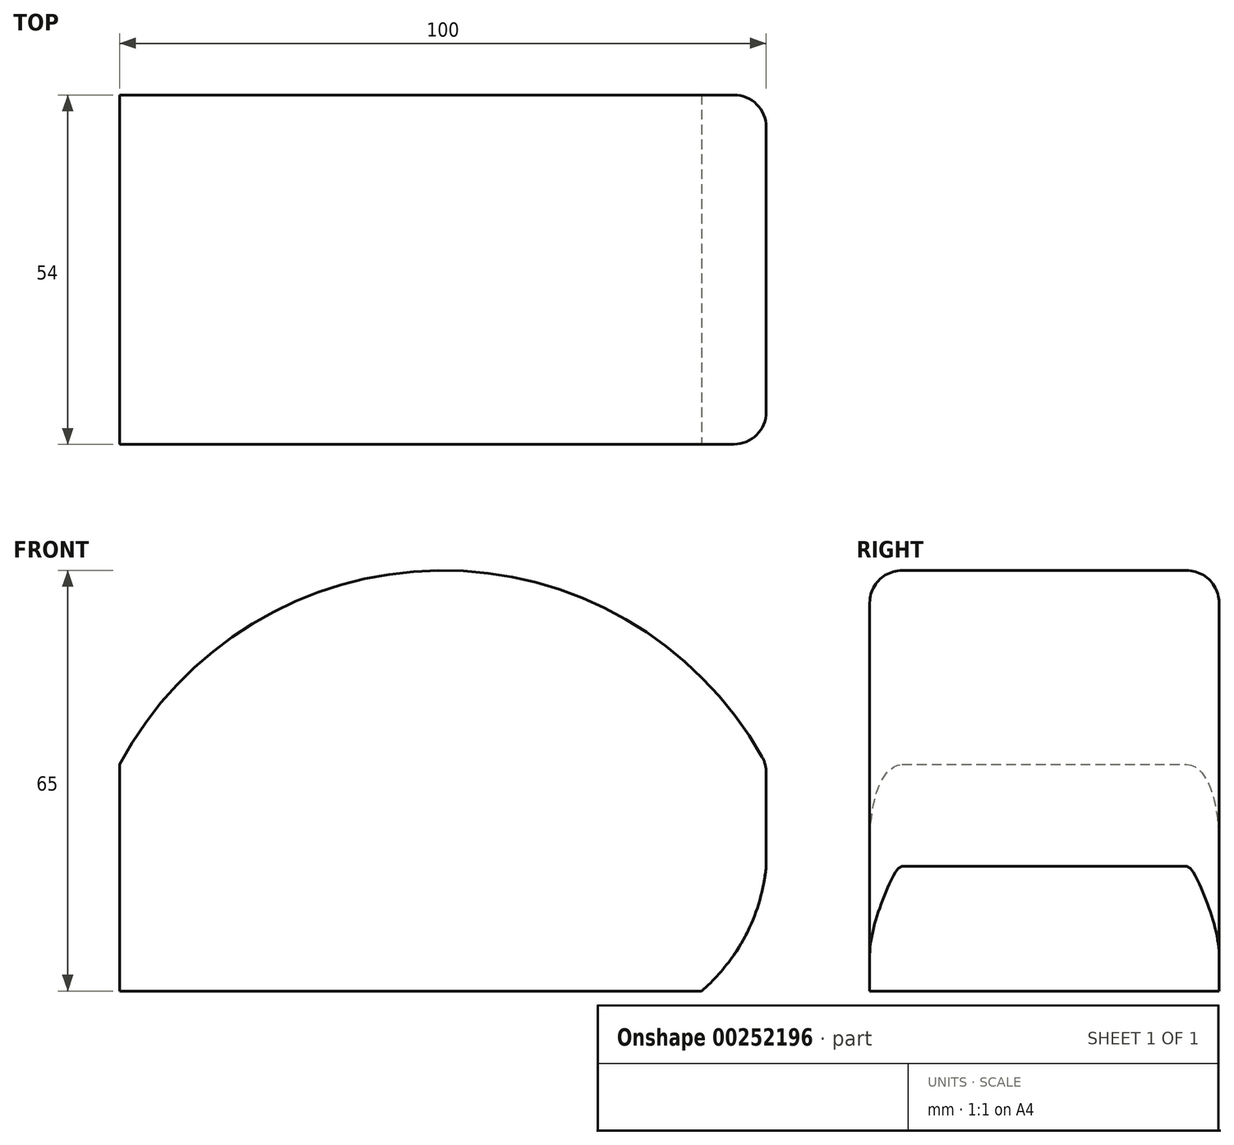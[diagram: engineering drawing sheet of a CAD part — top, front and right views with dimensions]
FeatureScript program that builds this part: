
annotation { "Feature Type Name" : "Feature", "Feature Type Description" : "" }
export const myFeature = defineFeature(function(context is Context, id is Id, definition is map)
    precondition{}
    {
        {
            var Q0;
            Q0=qCreatedBy(makeId("Front.planeOp"),FACE);
            var sketch = newSketch(context, id + "F0", { "sketchPlane" : qUnion([Q0])});
            skArc(sketch, "E0", {"start": v(50, 0) * mm, "mid": v(0, 30) * mm, "end": v(-50, 0) * mm});
            skLineSegment(sketch, "E1", {"start": v(0, 0) * mm, "end": v(-50, 0) * mm, "construction": true});
            skLineSegment(sketch, "E2", {"start": v(0, 0) * mm, "end": v(50, 0) * mm, "construction": true});
            skLineSegment(sketch, "E3", {"start": v(-50, 0) * mm, "end": v(50, 0) * mm});
            skSolve(sketch);
        }
        {
            var Q0;
            Q0 = qSketchRegion(id + "F0", true);
            extrude(context, id + "F1", {"entities" : qUnion([Q0]), "endBound" : BoundingType.SYMMETRIC, "depth" : 54 * mm});
        }
        {
            var Q0;
            Q0=makeQuery(id+"F1.opExtrude","SWEPT_FACE",FACE,{"disambiguationData":[OSD([sQuery(id+"F0.wireOp",EDGE,"E3")])]});
            extrude(context, id + "F2", {"entities" : qUnion([Q0]), "operationType" : NewBodyOperationType.ADD, "depth" : 35 * mm});
        }
        {
            var Q0;
            {var subQ0=sQuery(id+"F0.wireOp",EDGE,"E3");Q0=makeQuery(id+"F2.boolean.opBoolean","MERGE",FACE,{"derivedFrom":[makeQuery(id+"F1.opExtrude","CAP_FACE",FACE,{"disambiguationData":[OSD([sQuery(id+"F0.wireOp",EDGE,"E0"),subQ0])],"isStart":false}),makeQuery(id+"F2.opExtrude","SWEPT_FACE",FACE,{"disambiguationData":[OSD([subQ0]),TDD([makeQuery(id+"F1.opExtrude","CAP_EDGE",EDGE,{"disambiguationData":[OSD([subQ0])],"isStart":false})])]})]});}
            var sketch = newSketch(context, id + "F3", { "sketchPlane" : qUnion([Q0])});
            skArc(sketch, "E4", {"start": v(40, -35) * mm, "mid": v(48.05, -23.72) * mm, "end": v(50, -10) * mm});
            skSolve(sketch);
        }
        {
            var Q0;
            Q0 = qSketchRegion(id + "F3", true);
            var Q1;
            {var subQ0=sQuery(id+"F3.wireOp",EDGE,"E4");var subQ1=sQuery(id+"F0.wireOp",EDGE,"E3");var subQ2=makeQuery(id+"F2.opExtrude","CAP_EDGE",EDGE,{"disambiguationData":[OSD([subQ1]),TDD([makeQuery(id+"F1.opExtrude","CAP_EDGE",EDGE,{"disambiguationData":[OSD([subQ1])],"isStart":false})])],"isStart":false});var subQ3=makeQuery(id+"F3.imprint","INTERSECT",VERTEX,{"derivedFrom":[subQ2,subQ0]});Q1=makeQuery(id+"F3.imprint","IMPRINT",FACE,{"disambiguationData":[TD([[makeQuery(id+"F3.imprint","IMPRINT",EDGE,{"disambiguationData":[TD([[subQ3,-1.0]])],"derivedFrom":subQ0}),-1.0]])]});}
            extrude(context, id + "F4", {"entities" : qUnion([Q0, Q1]), "operationType" : NewBodyOperationType.REMOVE, "oppositeDirection" : true, "depth" : 54 * mm});
        }
        {
            var Q0;
            {var subQ0=sQuery(id+"F0.wireOp",EDGE,"E3");var subQ1=sQuery(id+"F0.wireOp",EDGE,"E0");var subQ2=makeQuery(id+"F1.opExtrude","SWEPT_EDGE",EDGE,{"disambiguationData":[OSD([subQ1,subQ0]),TDD([makeQuery(id+"F0.imprint","INTERSECT",VERTEX,{"disambiguationData":[OD(0.0)],"derivedFrom":[subQ1,subQ0]})])]});Q0=makeQuery(id+"F2.boolean.opBoolean","MERGE",EDGE,{"derivedFrom":[subQ2,makeQuery(id+"F2.opExtrude","CAP_EDGE",EDGE,{"disambiguationData":[OSD([subQ1,subQ0]),TDD([subQ2])],"isStart":true})]});}
            fillet(context, id + "F5", {"entities" : qUnion([Q0]), "radius" : 5 * mm, "tangentPropagation" : true, "allowEdgeOverflow" : false});
        }
        {
            var Q0;
            {var subQ0=sQuery(id+"F0.wireOp",EDGE,"E3");var subQ1=sQuery(id+"F0.wireOp",EDGE,"E0");Q0=makeQuery(id+"F2.opExtrude","SWEPT_EDGE",EDGE,{"disambiguationData":[OSD([subQ1,subQ0]),TDD([makeQuery(id+"F1.opExtrude","CAP_VERTEX",VERTEX,{"disambiguationData":[OSD([subQ1,subQ0]),TDD([makeQuery(id+"F0.imprint","INTERSECT",VERTEX,{"disambiguationData":[OD(0.0)],"derivedFrom":[subQ1,subQ0]})])],"isStart":true})])]});}
            var Q1;
            Q1=makeQuery(id+"F4.boolean.opBoolean","COPY",EDGE,{"derivedFrom":makeQuery(id+"F4.opExtrude","CAP_EDGE",EDGE,{"disambiguationData":[OSD([sQuery(id+"F3.wireOp",EDGE,"E4")])],"isStart":false})});
            fillet(context, id + "F6", {"entities" : qUnion([Q0, Q1]), "radius" : 5 * mm, "tangentPropagation" : true, "allowEdgeOverflow" : false});
        }
        {
            var Q0;
            Q0=makeQuery(id+"F1.opExtrude","CAP_EDGE",EDGE,{"disambiguationData":[OSD([sQuery(id+"F0.wireOp",EDGE,"E0")])],"isStart":false});
            var Q1;
            {var subQ0=sQuery(id+"F0.wireOp",EDGE,"E3");var subQ1=sQuery(id+"F0.wireOp",EDGE,"E0");Q1=makeQuery(id+"F2.opExtrude","SWEPT_EDGE",EDGE,{"disambiguationData":[OSD([subQ1,subQ0]),TDD([makeQuery(id+"F1.opExtrude","CAP_VERTEX",VERTEX,{"disambiguationData":[OSD([subQ1,subQ0]),TDD([makeQuery(id+"F0.imprint","INTERSECT",VERTEX,{"disambiguationData":[OD(0.0)],"derivedFrom":[subQ1,subQ0]})])],"isStart":false})])]});}
            var Q2;
            {var subQ0=sQuery(id+"F0.wireOp",EDGE,"E3");var subQ1=sQuery(id+"F0.wireOp",EDGE,"E0");var subQ2=makeQuery(id+"F1.opExtrude","SWEPT_EDGE",EDGE,{"disambiguationData":[OSD([subQ1,subQ0]),TDD([makeQuery(id+"F0.imprint","INTERSECT",VERTEX,{"disambiguationData":[OD(0.0)],"derivedFrom":[subQ1,subQ0]})])]});Q2=makeQuery(id+"F5.opFillet","BLEND_EDGE",EDGE,{"blendedFrom":[makeQuery(id+"F2.boolean.opBoolean","MERGE",EDGE,{"derivedFrom":[subQ2,makeQuery(id+"F2.opExtrude","CAP_EDGE",EDGE,{"disambiguationData":[OSD([subQ1,subQ0]),TDD([subQ2])],"isStart":true})]}),makeQuery(id+"F2.boolean.opBoolean","MERGE",FACE,{"derivedFrom":[makeQuery(id+"F1.opExtrude","CAP_FACE",FACE,{"disambiguationData":[OSD([subQ1,subQ0])],"isStart":false}),makeQuery(id+"F2.opExtrude","SWEPT_FACE",FACE,{"disambiguationData":[OSD([subQ0]),TDD([makeQuery(id+"F1.opExtrude","CAP_EDGE",EDGE,{"disambiguationData":[OSD([subQ0])],"isStart":false})])]})]})],"blendedInto":[makeQuery(id+"F2.boolean.opBoolean","MERGE",FACE,{"derivedFrom":[makeQuery(id+"F1.opExtrude","CAP_FACE",FACE,{"disambiguationData":[OSD([subQ1,subQ0])],"isStart":false}),makeQuery(id+"F2.opExtrude","SWEPT_FACE",FACE,{"disambiguationData":[OSD([subQ0]),TDD([makeQuery(id+"F1.opExtrude","CAP_EDGE",EDGE,{"disambiguationData":[OSD([subQ0])],"isStart":false})])]})]})]});}
            var Q3;
            Q3=makeQuery(id+"F4.boolean.opBoolean","COPY",EDGE,{"derivedFrom":makeQuery(id+"F4.opExtrude","CAP_EDGE",EDGE,{"disambiguationData":[OSD([sQuery(id+"F3.wireOp",EDGE,"E4")])],"isStart":true})});
            fillet(context, id + "F7", {"entities" : qUnion([Q0, Q1, Q2, Q3]), "radius" : 5 * mm, "tangentPropagation" : true, "allowEdgeOverflow" : false});
        }
    });
